# Revit family: Hager-Volta-IP30-syst-CH-fr
name_source: partatom
category: Electrical Equipment
units: mm (PartAtom-declared; Revit-internal decimal feet)

## family parameters
Cut with Voids When Loaded = No
Host = Face
Panel Configuration = Two Columns, Circuits Across
Part Type = Panelboard
Room Calculation Point = No
Round Connector Dimension = Use Diameter
Shared = No

## types (4) — shared parameters
EF000003 - mode de pose = EV000384 - saillie
EF000008 - largeur = 305 mm  [stored 1.00066 ft]
EF000049 - profondeur = 97 mm  [stored 0.318241 ft]
EF000118 - avec cadre/support de montage = No
EF001062 - finition CEM = No
EF001088 - possibilité de montage en saillie = No
EF001134 - rail DIN = No
EF001596 - matériau du boîtier/corps = EV000139 - plastique
EF002950 - largeur en nombre de modules = 12
EF004462 - type de fermeture = EV000154 - autre
EF005474 - indice de protection (IP) = EV006410 - IP30
EF006244 - couvercle/porte transparent(e) = Yes
EF006306 - avec serrure = No
EF015776 - borne de mise à la terre = No
EF015777 - borne à conducteur neutre = No
EF015941 - porte pour transmission du signal = No
HG000001 - nombre de colonnes = 1
HG000002 - avec porte = Yes
HG000003 - Gamme = Volta
HG000005 - Epaisseur = 3 mm  [stored 0.00984252 ft]
HG000006 - Encastré = No
HG000009 - Porte à double battant = No
HG000010 - Portes asymétriques = No
HG000011 - Rangées du bas vides = No
HG000017 - Distance entre pôles = 18 mm  [stored 0.0590551 ft]
Manufacturer = Hager
Type Comments = Volta
zero-valued in all types: Default Elevation, EF000218 - profondeur d'encastrement, EF000332 - hauteur d'encastrement, EF000846 - largeur d'encastrement, EF001131 - profondeur intérieure, HG000007 - Nombre de colonnes vides, HG000008 - Nombre de rangées vides

## per-type parameters (varying)
| type | EF000040 - hauteur | EF000116 - numéro RAL | EF000266 - nombre de rangées | HG000004 - Référence fabricant | Model |
| Saillie IP30 L305 H245 P97 12 Modules - G44037035 | 245 mm | 7035 | 1 | G44037035 | G44037035 |
| Saillie IP30 L305 H245 P97 12 Modules - G44039010 | 245 mm | 9010 | 1 | G44039010 | G44039010 |
| Saillie IP30 L305 H370 P97 12 Modules - G44047035 | 370 mm  [stored 1.21391 ft] | 7035 | 2 | G44047035 | G44047035 |
| Saillie IP30 L305 H370 P97 12 Modules - G44049010 | 370 mm  [stored 1.21391 ft] | 9010 | 2 | G44049010 | G44049010 |

note: [stored X ft] marks values corroborated as IEEE doubles in the binary element streams (Revit-internal decimal feet)

## geometry (parser evidence)
native form markers: Sweep x17
no freeform markers — native parametric forms only
